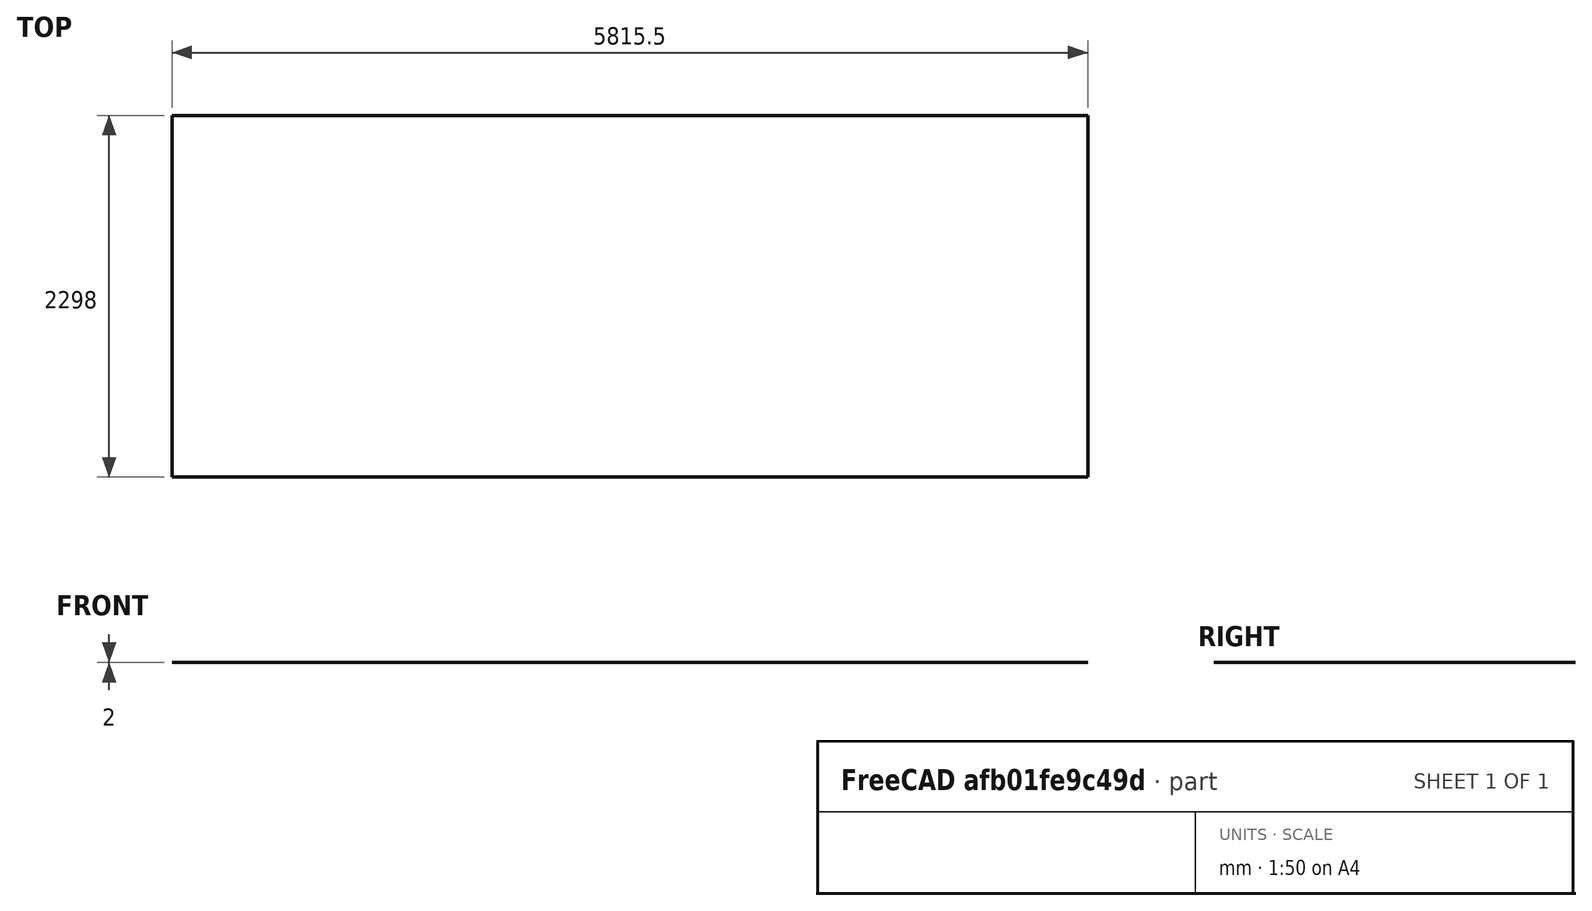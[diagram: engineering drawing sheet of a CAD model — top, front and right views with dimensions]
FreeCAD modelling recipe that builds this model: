
FCSTD DOCUMENT  (FreeCAD 0.18R4 (GitTag))
Label: plate-thin_bottom
License: All rights reserved
LicenseURL: http://en.wikipedia.org/wiki/All_rights_reserved
objects: Sketcher::SketchObject×1, PartDesign::Pad×1, PartDesign::Body×1
note: 4 computed .brp shape members not serialized (recipe doc carries the construction recipe); baked Part::Feature solids carry a one-line shape summary decoded from their .brp

FEATURE [Sketcher::SketchObject] Sketch
  MapMode = 5
  Support = -> [XY_Plane]
  sketch-geometry (4):
    g0: LineSegment StartX=-2907.75 StartY=1149 StartZ=0 EndX=2907.75 EndY=1149 EndZ=0
    g1: LineSegment StartX=2907.75 StartY=1149 StartZ=0 EndX=2907.75 EndY=-1149 EndZ=0
    g2: LineSegment StartX=2907.75 StartY=-1149 StartZ=0 EndX=-2907.75 EndY=-1149 EndZ=0
    g3: LineSegment StartX=-2907.75 StartY=-1149 StartZ=0 EndX=-2907.75 EndY=1149 EndZ=0
  constraints (12):
    c: Coincident(g0,g1)
    c: Coincident(g1,g2)
    c: Coincident(g2,g3)
    c: Coincident(g3,g0)
    c: Horizontal(g0)
    c: Horizontal(g2)
    c: Vertical(g1)
    c: Vertical(g3)
    c: DistanceX(g0,g0) = 5815.5
    c: DistanceY(g3,g3) = 2298
    c: DistanceX(g-1,g0) = 2907.75
    c: DistanceY(g-1,g0) = 1149
FEATURE [PartDesign::Pad] Pad
  Length = 2
  Length2 = 100
  Profile = -> Sketch
  Refine = true
  Type = 0
FEATURE [PartDesign::Body] Body
  Group = -> [Sketch,Pad]
  Origin = -> Origin
  Tip = -> Pad
